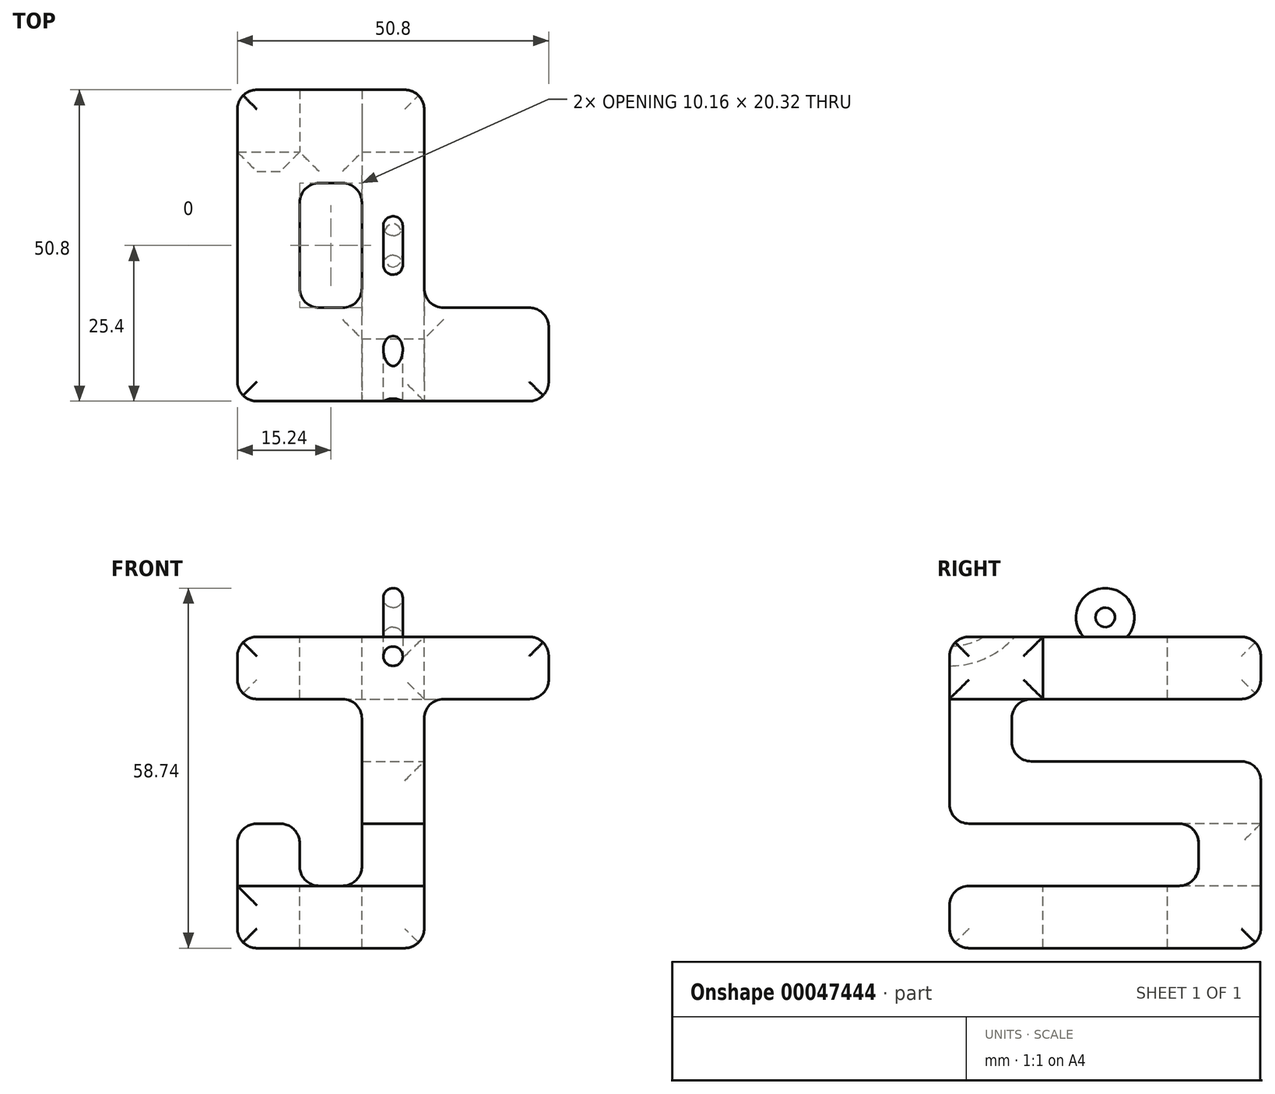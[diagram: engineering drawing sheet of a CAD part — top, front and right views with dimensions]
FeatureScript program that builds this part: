
annotation { "Feature Type Name" : "Feature", "Feature Type Description" : "" }
export const myFeature = defineFeature(function(context is Context, id is Id, definition is map)
    precondition{}
    {
        {
            var Q0;
            Q0=qCreatedBy(makeId("Front.planeOp"),FACE);
            var sketch = newSketch(context, id + "F0", { "sketchPlane" : qUnion([Q0])});
            skLineSegment(sketch, "E0.bottom", {"start": v(0, 0) * mm, "end": v(50.8, 0) * mm});
            skLineSegment(sketch, "E0.top", {"start": v(0, 50.8) * mm, "end": v(50.8, 50.8) * mm});
            skLineSegment(sketch, "E0.left", {"start": v(0, 0) * mm, "end": v(0, 50.8) * mm});
            skLineSegment(sketch, "E0.right", {"start": v(50.8, 0) * mm, "end": v(50.8, 50.8) * mm});
            skSolve(sketch);
        }
        {
            var Q0;
            Q0=makeQuery(id+"F0.imprint","IMPRINT",FACE,{"disambiguationData":[TD([[makeQuery(id+"F0.imprint","IMPRINT",EDGE,{"derivedFrom":sQuery(id+"F0.wireOp",EDGE,"E0.bottom")}),1.0]])]});
            extrude(context, id + "F1", {"entities" : qUnion([Q0]), "depth" : 50.8 * mm});
        }
        {
            var Q0;
            Q0=makeQuery(id+"F1.opExtrude","SWEPT_FACE",FACE,{"disambiguationData":[OSD([sQuery(id+"F0.wireOp",EDGE,"E0.right")])]});
            var sketch = newSketch(context, id + "F2", { "sketchPlane" : qUnion([Q0])});
            skLineSegment(sketch, "E1", {"start": v(-3.18, 50.8) * mm, "end": v(-47.63, 50.8) * mm});
            skLineSegment(sketch, "E2", {"start": v(-50.8, 47.62) * mm, "end": v(-50.8, 37.23) * mm});
            skLineSegment(sketch, "E3", {"start": v(0, 47.62) * mm, "end": v(0, 43.81) * mm});
            skLineSegment(sketch, "E4", {"start": v(-3.18, 40.64) * mm, "end": v(-37.47, 40.64) * mm});
            skLineSegment(sketch, "E5", {"start": v(-40.64, 37.46) * mm, "end": v(-40.64, 33.65) * mm});
            skLineSegment(sketch, "E6", {"start": v(-37.47, 30.48) * mm, "end": v(-3.18, 30.48) * mm});
            skLineSegment(sketch, "E7", {"start": v(0, 27.3) * mm, "end": v(0, 3.17) * mm});
            skLineSegment(sketch, "E8", {"start": v(-3.18, 0) * mm, "end": v(-47.63, 0) * mm});
            skLineSegment(sketch, "E9", {"start": v(-50.8, 3.17) * mm, "end": v(-50.8, 6.98) * mm});
            skLineSegment(sketch, "E10", {"start": v(-47.63, 10.16) * mm, "end": v(-13.33, 10.16) * mm});
            skLineSegment(sketch, "E11", {"start": v(-10.16, 13.33) * mm, "end": v(-10.16, 17.14) * mm});
            skLineSegment(sketch, "E12", {"start": v(-13.34, 20.32) * mm, "end": v(-47.63, 20.32) * mm});
            skPoint(sketch, "E12.endSnap0", {"position": v(-50.8, 25.4) * mm});
            skLineSegment(sketch, "E13", {"start": v(-50.8, 23.5) * mm, "end": v(-50.8, 37.23) * mm});
            skPoint(sketch, "E14.visualSharp", {"position": v(-50.8, 50.8) * mm});
            skArc(sketch, "E14.filletArc", {"start": v(-47.63, 50.8) * mm, "mid": v(-49.87, 49.87) * mm, "end": v(-50.8, 47.62) * mm});
            skPoint(sketch, "E15.visualSharp", {"position": v(0, 50.8) * mm});
            skArc(sketch, "E15.filletArc", {"start": v(0, 47.62) * mm, "mid": v(-0.93, 49.87) * mm, "end": v(-3.18, 50.8) * mm});
            skPoint(sketch, "E16.visualSharp", {"position": v(0, 40.64) * mm});
            skArc(sketch, "E16.filletArc", {"start": v(-3.18, 40.64) * mm, "mid": v(-0.93, 41.57) * mm, "end": v(0, 43.81) * mm});
            skPoint(sketch, "E17.visualSharp", {"position": v(-40.64, 40.64) * mm});
            skArc(sketch, "E17.filletArc", {"start": v(-37.47, 40.64) * mm, "mid": v(-39.71, 39.71) * mm, "end": v(-40.64, 37.46) * mm});
            skPoint(sketch, "E18.visualSharp", {"position": v(-40.64, 30.48) * mm});
            skArc(sketch, "E18.filletArc", {"start": v(-40.64, 33.65) * mm, "mid": v(-39.71, 31.4) * mm, "end": v(-37.47, 30.48) * mm});
            skPoint(sketch, "E19.visualSharp", {"position": v(0, 30.48) * mm});
            skArc(sketch, "E19.filletArc", {"start": v(0, 27.3) * mm, "mid": v(-0.93, 29.55) * mm, "end": v(-3.18, 30.48) * mm});
            skPoint(sketch, "E20.visualSharp", {"position": v(0, 0) * mm});
            skArc(sketch, "E20.filletArc", {"start": v(-3.18, 0) * mm, "mid": v(-0.93, 0.93) * mm, "end": v(0, 3.17) * mm});
            skPoint(sketch, "E21.visualSharp", {"position": v(-50.8, 0) * mm});
            skArc(sketch, "E21.filletArc", {"start": v(-50.8, 3.17) * mm, "mid": v(-49.87, 0.93) * mm, "end": v(-47.63, 0) * mm});
            skPoint(sketch, "E22.visualSharp", {"position": v(-50.8, 10.16) * mm});
            skArc(sketch, "E22.filletArc", {"start": v(-47.63, 10.16) * mm, "mid": v(-49.87, 9.23) * mm, "end": v(-50.8, 6.98) * mm});
            skPoint(sketch, "E23.visualSharp", {"position": v(-10.16, 10.16) * mm});
            skArc(sketch, "E23.filletArc", {"start": v(-13.33, 10.16) * mm, "mid": v(-11.09, 11.09) * mm, "end": v(-10.16, 13.33) * mm});
            skPoint(sketch, "E24.visualSharp", {"position": v(-10.16, 20.32) * mm});
            skArc(sketch, "E24.filletArc", {"start": v(-10.16, 17.14) * mm, "mid": v(-11.09, 19.4) * mm, "end": v(-13.34, 20.32) * mm});
            skPoint(sketch, "E25.visualSharp", {"position": v(-50.8, 20.32) * mm});
            skArc(sketch, "E25.filletArc", {"start": v(-50.8, 23.5) * mm, "mid": v(-49.87, 21.25) * mm, "end": v(-47.63, 20.32) * mm});
            skSolve(sketch);
        }
        {
            var Q0;
            Q0=makeQuery(id+"F2.imprint","IMPRINT",FACE,{"disambiguationData":[TD([[makeQuery(id+"F2.imprint","IMPRINT",EDGE,{"derivedFrom":sQuery(id+"F2.wireOp",EDGE,"E4")}),1.0]])]});
            var Q1;
            Q1=makeQuery(id+"F2.imprint","IMPRINT",FACE,{"disambiguationData":[TD([[makeQuery(id+"F2.imprint","IMPRINT",EDGE,{"derivedFrom":sQuery(id+"F2.wireOp",EDGE,"E10")}),1.0]])]});
            var Q2;
            {var subQ2=sQuery(id+"F2.wireOp",EDGE,"E15.filletArc");Q2=makeQuery(id+"F2.imprint","IMPRINT",FACE,{"disambiguationData":[TD([[makeQuery(id+"F2.imprint","IMPRINT",EDGE,{"derivedFrom":subQ2}),-1.0]])]});}
            var Q3;
            {var subQ2=sQuery(id+"F2.wireOp",EDGE,"E14.filletArc");Q3=makeQuery(id+"F2.imprint","IMPRINT",FACE,{"disambiguationData":[TD([[makeQuery(id+"F2.imprint","IMPRINT",EDGE,{"derivedFrom":subQ2}),-1.0]])]});}
            var Q4;
            {var subQ2=sQuery(id+"F2.wireOp",EDGE,"E20.filletArc");Q4=makeQuery(id+"F2.imprint","IMPRINT",FACE,{"disambiguationData":[TD([[makeQuery(id+"F2.imprint","IMPRINT",EDGE,{"derivedFrom":subQ2}),-1.0]])]});}
            var Q5;
            {var subQ2=sQuery(id+"F2.wireOp",EDGE,"E21.filletArc");Q5=makeQuery(id+"F2.imprint","IMPRINT",FACE,{"disambiguationData":[TD([[makeQuery(id+"F2.imprint","IMPRINT",EDGE,{"derivedFrom":subQ2}),-1.0]])]});}
            extrude(context, id + "F3", {"entities" : qUnion([Q0, Q1, Q2, Q3, Q4, Q5]), "operationType" : NewBodyOperationType.REMOVE, "endBound" : BoundingType.THROUGH_ALL, "oppositeDirection" : true, "depth" : 25.4 * mm});
        }
        {
            var Q0;
            Q0=qCreatedBy(makeId("Top.planeOp"),FACE);
            cPlane(context, id + "F4", {"entities" : qUnion([Q0]), "cplaneType" : CPlaneType.OFFSET, "offset" : 50.8 * mm, "width" : 152.4 * mm, "height" : 152.4 * mm});
        }
        {
            var Q0;
            Q0=qCreatedBy(makeId("Front.planeOp"),FACE);
            cPlane(context, id + "F5", {"entities" : qUnion([Q0]), "cplaneType" : CPlaneType.OFFSET, "offset" : 50.8 * mm, "width" : 152.4 * mm, "height" : 152.4 * mm});
        }
        {
            var Q0;
            Q0=qCreatedBy(id+"F5.planeOp",FACE);
            var sketch = newSketch(context, id + "F6", { "sketchPlane" : qUnion([Q0])});
            skLineSegment(sketch, "E26", {"start": v(0, 43.81) * mm, "end": v(0, 47.63) * mm});
            skLineSegment(sketch, "E27", {"start": v(3.18, 50.8) * mm, "end": v(47.62, 50.8) * mm});
            skLineSegment(sketch, "E28", {"start": v(50.8, 47.63) * mm, "end": v(50.8, 43.81) * mm});
            skLineSegment(sketch, "E29", {"start": v(27.3, 0) * mm, "end": v(3.18, 0) * mm});
            skLineSegment(sketch, "E30", {"start": v(13.34, 10.16) * mm, "end": v(17.15, 10.16) * mm});
            skLineSegment(sketch, "E31", {"start": v(20.32, 13.34) * mm, "end": v(20.32, 37.47) * mm});
            skLineSegment(sketch, "E32", {"start": v(17.15, 40.64) * mm, "end": v(3.18, 40.64) * mm});
            skLineSegment(sketch, "E33", {"start": v(30.48, 3.18) * mm, "end": v(30.48, 37.47) * mm});
            skLineSegment(sketch, "E34", {"start": v(33.65, 40.64) * mm, "end": v(47.63, 40.64) * mm});
            skLineSegment(sketch, "E35", {"start": v(0, 10.16) * mm, "end": v(0, 17.15) * mm});
            skLineSegment(sketch, "E36", {"start": v(3.18, 20.32) * mm, "end": v(6.99, 20.32) * mm});
            skLineSegment(sketch, "E37", {"start": v(10.16, 17.15) * mm, "end": v(10.16, 13.33) * mm});
            skPoint(sketch, "E38.visualSharp", {"position": v(0, 50.8) * mm});
            skArc(sketch, "E38.filletArc", {"start": v(3.17, 50.8) * mm, "mid": v(0.93, 49.87) * mm, "end": v(0, 47.63) * mm});
            skPoint(sketch, "E39.newPointA", {"position": v(0, 0) * mm});
            skArc(sketch, "E39.filletArc", {"start": v(0, 43.81) * mm, "mid": v(0.93, 41.57) * mm, "end": v(3.18, 40.64) * mm});
            skPoint(sketch, "E40.visualSharp", {"position": v(20.32, 40.64) * mm});
            skArc(sketch, "E40.filletArc", {"start": v(20.32, 37.47) * mm, "mid": v(19.4, 39.71) * mm, "end": v(17.15, 40.64) * mm});
            skPoint(sketch, "E41.visualSharp", {"position": v(20.32, 10.16) * mm});
            skArc(sketch, "E41.filletArc", {"start": v(17.15, 10.16) * mm, "mid": v(19.4, 11.09) * mm, "end": v(20.32, 13.34) * mm});
            skPoint(sketch, "E42.visualSharp", {"position": v(10.16, 10.16) * mm});
            skArc(sketch, "E42.filletArc", {"start": v(10.16, 13.33) * mm, "mid": v(11.09, 11.09) * mm, "end": v(13.34, 10.16) * mm});
            skPoint(sketch, "E43.visualSharp", {"position": v(10.16, 20.32) * mm});
            skArc(sketch, "E43.filletArc", {"start": v(10.16, 17.15) * mm, "mid": v(9.23, 19.4) * mm, "end": v(6.99, 20.32) * mm});
            skPoint(sketch, "E44.visualSharp", {"position": v(0, 20.32) * mm});
            skArc(sketch, "E44.filletArc", {"start": v(3.18, 20.32) * mm, "mid": v(0.93, 19.4) * mm, "end": v(0, 17.15) * mm});
            skArc(sketch, "E45.filletArc", {"start": v(27.3, 0) * mm, "mid": v(29.55, 0.93) * mm, "end": v(30.48, 3.18) * mm});
            skPoint(sketch, "E46.visualSharp", {"position": v(30.48, 40.64) * mm});
            skArc(sketch, "E46.filletArc", {"start": v(33.65, 40.64) * mm, "mid": v(31.4, 39.71) * mm, "end": v(30.48, 37.47) * mm});
            skPoint(sketch, "E47.newPointB", {"position": v(50.8, 0) * mm});
            skArc(sketch, "E47.filletArc", {"start": v(47.63, 40.64) * mm, "mid": v(49.87, 41.57) * mm, "end": v(50.8, 43.81) * mm});
            skPoint(sketch, "E48.visualSharp", {"position": v(50.8, 50.8) * mm});
            skArc(sketch, "E48.filletArc", {"start": v(50.8, 47.63) * mm, "mid": v(49.87, 49.87) * mm, "end": v(47.62, 50.8) * mm});
            skLineSegment(sketch, "E49", {"start": v(0, 10.16) * mm, "end": v(0, 3.18) * mm});
            skArc(sketch, "E50.filletArc", {"start": v(0, 3.18) * mm, "mid": v(0.93, 0.93) * mm, "end": v(3.18, 0) * mm});
            skLineSegment(sketch, "E51", {"start": v(0, 47.63) * mm, "end": v(0, 50.8) * mm});
            skLineSegment(sketch, "E52", {"start": v(47.62, 50.8) * mm, "end": v(50.8, 50.8) * mm});
            skLineSegment(sketch, "E53", {"start": v(50.8, 47.63) * mm, "end": v(50.8, 50.8) * mm});
            skLineSegment(sketch, "E54", {"start": v(3.18, 0) * mm, "end": v(0, 0) * mm});
            skLineSegment(sketch, "E55", {"start": v(0, 3.18) * mm, "end": v(0, 0) * mm});
            skLineSegment(sketch, "E56", {"start": v(0, 43.81) * mm, "end": v(0, 17.15) * mm});
            skLineSegment(sketch, "E57", {"start": v(50.8, 43.81) * mm, "end": v(50.8, 0) * mm});
            skLineSegment(sketch, "E58", {"start": v(50.8, 0) * mm, "end": v(27.3, 0) * mm});
            skLineSegment(sketch, "E59", {"start": v(0, 50.8) * mm, "end": v(3.18, 50.8) * mm});
            skSolve(sketch);
        }
        {
            var Q0;
            Q0=makeQuery(id+"F6.imprint","IMPRINT",FACE,{"disambiguationData":[TD([[makeQuery(id+"F6.imprint","IMPRINT",EDGE,{"derivedFrom":sQuery(id+"F6.wireOp",EDGE,"E30")}),1.0]])]});
            var Q1;
            Q1=makeQuery(id+"F6.imprint","IMPRINT",FACE,{"disambiguationData":[TD([[makeQuery(id+"F6.imprint","IMPRINT",EDGE,{"derivedFrom":sQuery(id+"F6.wireOp",EDGE,"E48.filletArc")}),-1.0]])]});
            var Q2;
            Q2=makeQuery(id+"F6.imprint","IMPRINT",FACE,{"disambiguationData":[TD([[makeQuery(id+"F6.imprint","IMPRINT",EDGE,{"derivedFrom":sQuery(id+"F6.wireOp",EDGE,"E33")}),-1.0]])]});
            var Q3;
            Q3=makeQuery(id+"F6.imprint","IMPRINT",FACE,{"disambiguationData":[TD([[makeQuery(id+"F6.imprint","IMPRINT",EDGE,{"derivedFrom":sQuery(id+"F6.wireOp",EDGE,"E50.filletArc")}),-1.0]])]});
            var Q4;
            Q4=makeQuery(id+"F6.imprint","IMPRINT",FACE,{"disambiguationData":[TD([[makeQuery(id+"F6.imprint","IMPRINT",EDGE,{"derivedFrom":sQuery(id+"F6.wireOp",EDGE,"E38.filletArc")}),-1.0]])]});
            extrude(context, id + "F7", {"entities" : qUnion([Q0, Q1, Q2, Q3, Q4]), "operationType" : NewBodyOperationType.REMOVE, "endBound" : BoundingType.THROUGH_ALL, "oppositeDirection" : true, "depth" : 25.4 * mm});
        }
        {
            var Q0;
            Q0=qCreatedBy(id+"F4.planeOp",FACE);
            var sketch = newSketch(context, id + "F8", { "sketchPlane" : qUnion([Q0])});
            skLineSegment(sketch, "E60", {"start": v(0, -3.18) * mm, "end": v(0, -47.63) * mm});
            skLineSegment(sketch, "E61", {"start": v(3.18, -50.8) * mm, "end": v(47.63, -50.8) * mm});
            skLineSegment(sketch, "E62", {"start": v(50.8, -47.63) * mm, "end": v(50.8, -38.73) * mm});
            skLineSegment(sketch, "E63", {"start": v(27.3, 0) * mm, "end": v(3.18, 0) * mm});
            skLineSegment(sketch, "E64", {"start": v(47.63, -35.56) * mm, "end": v(33.66, -35.56) * mm});
            skLineSegment(sketch, "E65", {"start": v(30.48, -32.38) * mm, "end": v(30.48, -3.17) * mm});
            skLineSegment(sketch, "E66", {"start": v(20.32, -32.38) * mm, "end": v(20.32, -18.41) * mm});
            skLineSegment(sketch, "E67", {"start": v(17.14, -15.24) * mm, "end": v(13.34, -15.24) * mm});
            skLineSegment(sketch, "E68", {"start": v(10.16, -18.41) * mm, "end": v(10.16, -32.38) * mm});
            skLineSegment(sketch, "E69", {"start": v(13.34, -35.56) * mm, "end": v(17.15, -35.56) * mm});
            skPoint(sketch, "E70.visualSharp", {"position": v(0, -50.8) * mm});
            skArc(sketch, "E70.filletArc", {"start": v(0, -47.63) * mm, "mid": v(0.93, -49.87) * mm, "end": v(3.18, -50.8) * mm});
            skPoint(sketch, "E71.visualSharp", {"position": v(50.8, -50.8) * mm});
            skArc(sketch, "E71.filletArc", {"start": v(47.63, -50.8) * mm, "mid": v(49.87, -49.87) * mm, "end": v(50.8, -47.63) * mm});
            skPoint(sketch, "E72.newPointA", {"position": v(50.8, 0) * mm});
            skArc(sketch, "E72.filletArc", {"start": v(50.8, -38.73) * mm, "mid": v(49.87, -36.49) * mm, "end": v(47.63, -35.56) * mm});
            skPoint(sketch, "E73.visualSharp", {"position": v(30.48, -35.56) * mm});
            skArc(sketch, "E73.filletArc", {"start": v(30.48, -32.38) * mm, "mid": v(31.4, -34.63) * mm, "end": v(33.66, -35.56) * mm});
            skPoint(sketch, "E74.newPointA", {"position": v(30.48, 0) * mm});
            skArc(sketch, "E74.filletArc", {"start": v(30.48, -3.17) * mm, "mid": v(29.55, -0.93) * mm, "end": v(27.3, 0) * mm});
            skPoint(sketch, "E75.visualSharp", {"position": v(0, 0) * mm});
            skArc(sketch, "E75.filletArc", {"start": v(3.18, 0) * mm, "mid": v(0.93, -0.93) * mm, "end": v(0, -3.18) * mm});
            skPoint(sketch, "E76.visualSharp", {"position": v(10.16, -35.56) * mm});
            skArc(sketch, "E76.filletArc", {"start": v(10.16, -32.38) * mm, "mid": v(11.09, -34.63) * mm, "end": v(13.34, -35.56) * mm});
            skPoint(sketch, "E77.visualSharp", {"position": v(20.32, -35.56) * mm});
            skArc(sketch, "E77.filletArc", {"start": v(17.15, -35.56) * mm, "mid": v(19.4, -34.63) * mm, "end": v(20.32, -32.38) * mm});
            skPoint(sketch, "E78.visualSharp", {"position": v(20.32, -15.24) * mm});
            skArc(sketch, "E78.filletArc", {"start": v(20.32, -18.41) * mm, "mid": v(19.4, -16.17) * mm, "end": v(17.14, -15.24) * mm});
            skPoint(sketch, "E79.visualSharp", {"position": v(10.16, -15.24) * mm});
            skArc(sketch, "E79.filletArc", {"start": v(13.34, -15.24) * mm, "mid": v(11.09, -16.17) * mm, "end": v(10.16, -18.41) * mm});
            skLineSegment(sketch, "E80", {"start": v(3.18, -50.8) * mm, "end": v(0, -50.8) * mm});
            skLineSegment(sketch, "E81", {"start": v(0, -47.63) * mm, "end": v(0, -50.8) * mm});
            skLineSegment(sketch, "E82", {"start": v(0, -3.18) * mm, "end": v(0, 0) * mm});
            skLineSegment(sketch, "E83", {"start": v(3.18, 0) * mm, "end": v(0, 0) * mm});
            skLineSegment(sketch, "E84", {"start": v(27.3, 0) * mm, "end": v(50.8, 0) * mm});
            skLineSegment(sketch, "E85", {"start": v(50.8, -38.73) * mm, "end": v(50.8, 0) * mm});
            skLineSegment(sketch, "E86", {"start": v(50.8, -50.8) * mm, "end": v(47.63, -50.8) * mm});
            skLineSegment(sketch, "E87", {"start": v(50.8, -50.8) * mm, "end": v(50.8, -47.63) * mm});
            skSolve(sketch);
        }
        {
            var Q0;
            Q0=makeQuery(id+"F8.imprint","IMPRINT",FACE,{"disambiguationData":[TD([[makeQuery(id+"F8.imprint","IMPRINT",EDGE,{"derivedFrom":sQuery(id+"F8.wireOp",EDGE,"E70.filletArc")}),-1.0]])]});
            var Q1;
            Q1=makeQuery(id+"F8.imprint","IMPRINT",FACE,{"disambiguationData":[TD([[makeQuery(id+"F8.imprint","IMPRINT",EDGE,{"derivedFrom":sQuery(id+"F8.wireOp",EDGE,"E75.filletArc")}),-1.0]])]});
            var Q2;
            Q2=makeQuery(id+"F8.imprint","IMPRINT",FACE,{"disambiguationData":[TD([[makeQuery(id+"F8.imprint","IMPRINT",EDGE,{"derivedFrom":sQuery(id+"F8.wireOp",EDGE,"E71.filletArc")}),-1.0]])]});
            var Q3;
            Q3=makeQuery(id+"F8.imprint","IMPRINT",FACE,{"disambiguationData":[TD([[makeQuery(id+"F8.imprint","IMPRINT",EDGE,{"derivedFrom":sQuery(id+"F8.wireOp",EDGE,"E66")}),1.0]])]});
            var Q4;
            Q4=makeQuery(id+"F8.imprint","IMPRINT",FACE,{"disambiguationData":[TD([[makeQuery(id+"F8.imprint","IMPRINT",EDGE,{"derivedFrom":sQuery(id+"F8.wireOp",EDGE,"E64")}),-1.0]])]});
            extrude(context, id + "F9", {"entities" : qUnion([Q0, Q1, Q2, Q3, Q4]), "operationType" : NewBodyOperationType.REMOVE, "endBound" : BoundingType.THROUGH_ALL, "oppositeDirection" : true, "depth" : 25.4 * mm});
        }
        {
            var Q0;
            Q0=qCreatedBy(makeId("Front.planeOp"),FACE);
            cPlane(context, id + "F10", {"entities" : qUnion([Q0]), "cplaneType" : CPlaneType.OFFSET, "offset" : 25.4 * mm, "width" : 152.4 * mm, "height" : 152.4 * mm});
        }
        {
            var Q0;
            Q0=qCreatedBy(id+"F10.planeOp",FACE);
            var sketch = newSketch(context, id + "F11", { "sketchPlane" : qUnion([Q0])});
            skCircle(sketch, "E88", {"center": v(25.4, 50.8) * mm, "radius": 1.59 * mm});
            skLineSegment(sketch, "E89", {"start": v(0, 53.98) * mm, "end": v(60.8, 53.98) * mm});
            skSolve(sketch);
        }
        {
            var Q0;
            Q0 = qSketchRegion(id + "F11", true);
            var Q1;
            Q1=sQuery(id+"F11.wireOp",EDGE,"E89");
            revolve(context, id + "F12", {"operationType" : NewBodyOperationType.ADD, "entities" : qUnion([Q0]), "axis" : qUnion([Q1]), "revolveType" : RevolveType.FULL});
        }
        {
            var Q0;
            {var subQ0=sQuery(id+"F0.wireOp",EDGE,"E0.left");var subQ1=sQuery(id+"F0.wireOp",EDGE,"E0.right");Q0=makeQuery(id+"F3.boolean.opBoolean","SPLIT",FACE,{"disambiguationData":[TD([makeQuery(id+"F3.opExtrude","SWEPT_FACE",FACE,{"disambiguationData":[OSD([sQuery(id+"F2.wireOp",EDGE,"E14.filletArc")])]})])],"derivedFrom":makeQuery(id+"F1.opExtrude","CAP_FACE",FACE,{"disambiguationData":[OSD([sQuery(id+"F0.wireOp",EDGE,"E0.bottom"),sQuery(id+"F0.wireOp",EDGE,"E0.top"),subQ0,subQ1])],"isStart":false})});}
            var sketch = newSketch(context, id + "F13", { "sketchPlane" : qUnion([Q0])});
            skCircle(sketch, "E90", {"center": v(25.4, 47.62) * mm, "radius": 1.59 * mm});
            skPoint(sketch, "E90.centerSnap0", {"position": v(25.4, 47.62) * mm});
            skLineSegment(sketch, "E91", {"start": v(0, 60.32) * mm, "end": v(55, 60.32) * mm});
            skSolve(sketch);
        }
        {
            var Q0;
            {var subQ0=sQuery(id+"F13.wireOp",EDGE,"E90");var subQ1=makeQuery(id+"F3.boolean.opBoolean","COPY",EDGE,{"derivedFrom":makeQuery(id+"F3.opExtrude","SWEPT_EDGE",EDGE,{"disambiguationData":[OSD([sQuery(id+"F0.wireOp",EDGE,"E0.right"),sQuery(id+"F2.wireOp",EDGE,"E2"),sQuery(id+"F2.wireOp",EDGE,"E14.filletArc")])]})});var subQ2=makeQuery(id+"F13.imprint","INTERSECT",VERTEX,{"disambiguationData":[OD(0.0)],"derivedFrom":[subQ1,subQ0]});Q0=makeQuery(id+"F13.imprint","IMPRINT",FACE,{"disambiguationData":[TD([[makeQuery(id+"F13.imprint","IMPRINT",EDGE,{"disambiguationData":[TD([[subQ2,-1.0]])],"derivedFrom":subQ0}),1.0]])]});}
            var Q1;
            {var subQ0=sQuery(id+"F13.wireOp",EDGE,"E90");var subQ1=makeQuery(id+"F3.boolean.opBoolean","COPY",EDGE,{"derivedFrom":makeQuery(id+"F3.opExtrude","SWEPT_EDGE",EDGE,{"disambiguationData":[OSD([sQuery(id+"F0.wireOp",EDGE,"E0.right"),sQuery(id+"F2.wireOp",EDGE,"E2"),sQuery(id+"F2.wireOp",EDGE,"E14.filletArc")])]})});var subQ2=makeQuery(id+"F13.imprint","INTERSECT",VERTEX,{"disambiguationData":[OD(0.0)],"derivedFrom":[subQ1,subQ0]});Q1=makeQuery(id+"F13.imprint","IMPRINT",FACE,{"disambiguationData":[TD([[makeQuery(id+"F13.imprint","IMPRINT",EDGE,{"disambiguationData":[TD([[subQ2,1.0]])],"derivedFrom":subQ0}),1.0]])]});}
            var Q2;
            Q2=sQuery(id+"F13.wireOp",EDGE,"E91");
            revolve(context, id + "F14", {"operationType" : NewBodyOperationType.REMOVE, "entities" : qUnion([Q0, Q1]), "axis" : qUnion([Q2]), "revolveType" : RevolveType.FULL, "oppositeDirection" : true});
        }
    });
